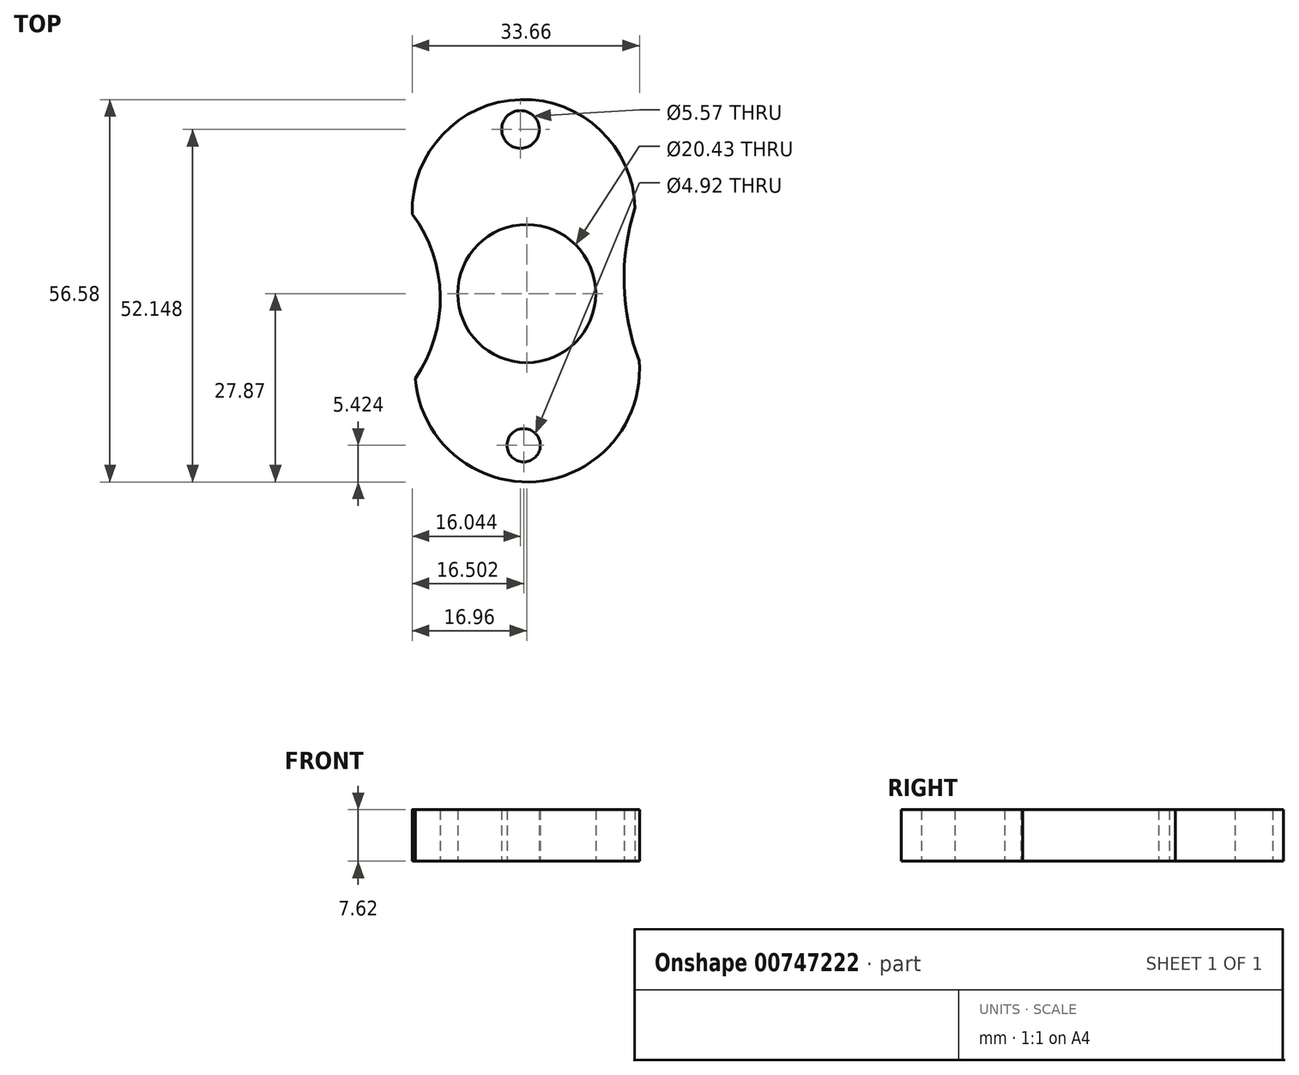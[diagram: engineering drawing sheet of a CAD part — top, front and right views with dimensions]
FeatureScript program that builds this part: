
annotation { "Feature Type Name" : "Feature", "Feature Type Description" : "" }
export const myFeature = defineFeature(function(context is Context, id is Id, definition is map)
    precondition{}
    {
        {
            var Q0;
            Q0=qCreatedBy(makeId("Top.planeOp"),FACE);
            var sketch = newSketch(context, id + "F0", { "sketchPlane" : qUnion([Q0])});
            skCircle(sketch, "E0", {"center": v(0, 0) * mm, "radius": 10.21 * mm});
            skArc(sketch, "E1", {"start": v(16.03, 12.67) * mm, "mid": v(-0.92, 28.7) * mm, "end": v(-16.95, 11.76) * mm});
            skArc(sketch, "E2", {"start": v(-16.5, -12.57) * mm, "mid": v(1.4, -27.82) * mm, "end": v(16.64, -9.92) * mm});
            skArc(sketch, "E3", {"start": v(-16.5, -12.57) * mm, "mid": v(-12.81, -0.33) * mm, "end": v(-16.95, 11.76) * mm});
            skArc(sketch, "E4", {"start": v(16.03, 12.67) * mm, "mid": v(14.42, 1.32) * mm, "end": v(16.64, -9.92) * mm});
            skCircle(sketch, "E5", {"center": v(-0.92, 24.28) * mm, "radius": 2.79 * mm});
            skPoint(sketch, "E5.centerSnap0", {"position": v(-0.92, 28.7) * mm});
            skCircle(sketch, "E6", {"center": v(-0.46, -22.45) * mm, "radius": 2.46 * mm});
            skSolve(sketch);
        }
        {
            var Q0;
            Q0 = qSketchRegion(id + "F0", true);
            extrude(context, id + "F1", {"entities" : qUnion([Q0]), "depth" : 7.62 * mm, "offsetDistance" : 25.4 * mm});
        }
    });
